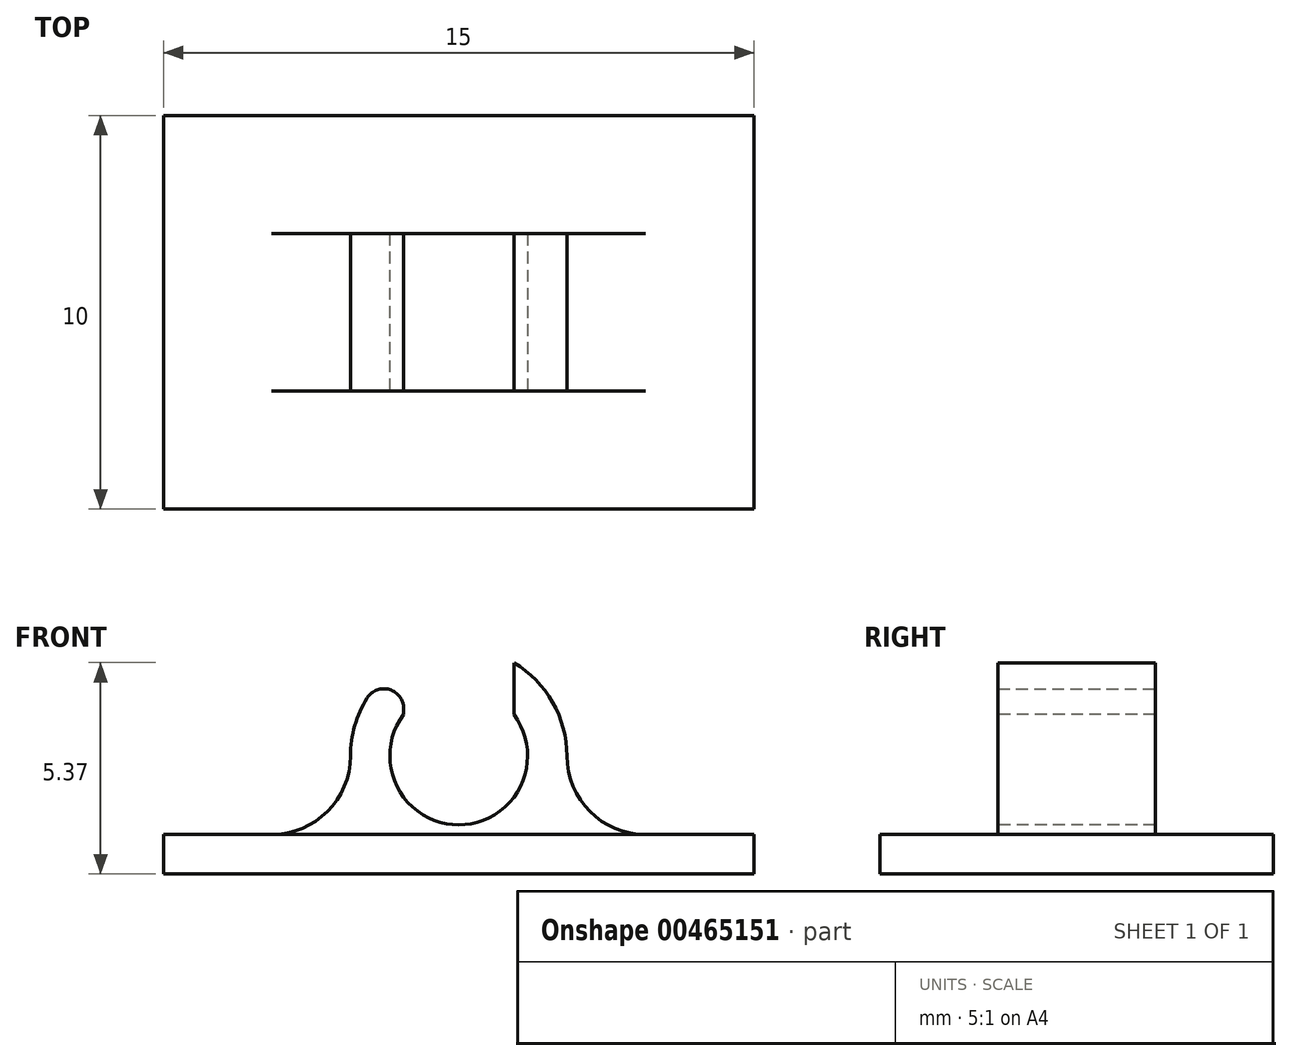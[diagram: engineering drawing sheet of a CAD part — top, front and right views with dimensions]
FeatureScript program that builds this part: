
annotation { "Feature Type Name" : "Feature", "Feature Type Description" : "" }
export const myFeature = defineFeature(function(context is Context, id is Id, definition is map)
    precondition{}
    {
        {
            assignVariable(context, id + "F0", {"name" : "base_height", "anyValue" : 1 * mm});
        }
        {
            var Q0;
            Q0=qCreatedBy(makeId("Top.planeOp"),FACE);
            var sketch = newSketch(context, id + "F1", { "sketchPlane" : qUnion([Q0])});
            skLineSegment(sketch, "E0.bottom", {"start": v(7.5, 5) * mm, "end": v(-7.5, 5) * mm});
            skLineSegment(sketch, "E0.top", {"start": v(7.5, -5) * mm, "end": v(-7.5, -5) * mm});
            skLineSegment(sketch, "E0.left", {"start": v(7.5, 5) * mm, "end": v(7.5, -5) * mm});
            skLineSegment(sketch, "E0.right", {"start": v(-7.5, 5) * mm, "end": v(-7.5, -5) * mm});
            skPoint(sketch, "E0.middle", {"position": v(0, 0) * mm});
            skSolve(sketch);
        }
        {
            var Q0;
            Q0=makeQuery(id+"F1.imprint","IMPRINT",FACE,{"disambiguationData":[TD([[makeQuery(id+"F1.imprint","IMPRINT",EDGE,{"derivedFrom":sQuery(id+"F1.wireOp",EDGE,"E0.bottom")}),1.0]])]});
            extrude(context, id + "F2", {"entities" : qUnion([Q0]), "depth" : getVariable(context, 'base_height')});
        }
        {
            var Q0;
            Q0=qCreatedBy(makeId("Front.planeOp"),FACE);
            var sketch = newSketch(context, id + "F3", { "sketchPlane" : qUnion([Q0])});
            skCircle(sketch, "E1", {"center": v(0, 3) * mm, "radius": 2.75 * mm});
            skSolve(sketch);
        }
        {
            var Q0;
            Q0=makeQuery(id+"F3.imprint","IMPRINT",FACE,{"disambiguationData":[TD([[makeQuery(id+"F3.imprint","IMPRINT",EDGE,{"derivedFrom":sQuery(id+"F3.wireOp",EDGE,"E1")}),1.0]])]});
            extrude(context, id + "F4", {"entities" : qUnion([Q0]), "operationType" : NewBodyOperationType.ADD, "endBound" : BoundingType.SYMMETRIC, "depth" : 4 * mm});
        }
        {
            var Q0;
            Q0=makeQuery(id+"F4.opExtrude","CAP_FACE",FACE,{"disambiguationData":[OSD([sQuery(id+"F3.wireOp",EDGE,"E1")])],"isStart":false});
            var sketch = newSketch(context, id + "F5", { "sketchPlane" : qUnion([Q0])});
            skCircle(sketch, "E2", {"center": v(0, 3) * mm, "radius": 1.75 * mm});
            skLineSegment(sketch, "E3.bottom", {"start": v(1.4, 6.4) * mm, "end": v(-1.4, 6.4) * mm});
            skLineSegment(sketch, "E3.top", {"start": v(1.4, 3.1) * mm, "end": v(-1.4, 3.1) * mm});
            skLineSegment(sketch, "E3.left", {"start": v(1.4, 6.4) * mm, "end": v(1.4, 3.1) * mm});
            skLineSegment(sketch, "E3.right", {"start": v(-1.4, 6.4) * mm, "end": v(-1.4, 3.1) * mm});
            skPoint(sketch, "E3.middle", {"position": v(0, 4.75) * mm});
            skSolve(sketch);
        }
        {
            var Q0;
            {var subQ5=sQuery(id+"F5.wireOp",EDGE,"E3.top");Q0=makeQuery(id+"F5.imprint","IMPRINT",FACE,{"disambiguationData":[TD([[makeQuery(id+"F5.imprint","IMPRINT",EDGE,{"derivedFrom":subQ5}),1.0]])]});}
            var Q1;
            {var subQ5=sQuery(id+"F5.wireOp",EDGE,"E3.top");Q1=makeQuery(id+"F5.imprint","IMPRINT",FACE,{"disambiguationData":[TD([[makeQuery(id+"F5.imprint","IMPRINT",EDGE,{"derivedFrom":subQ5}),-1.0]])]});}
            var Q2;
            {var subQ0=sQuery(id+"F5.wireOp",EDGE,"E3.left");var subQ1=sQuery(id+"F5.wireOp",EDGE,"E2");var subQ2=makeQuery(id+"F5.imprint","INTERSECT",VERTEX,{"derivedFrom":[subQ1,subQ0]});Q2=makeQuery(id+"F5.imprint","IMPRINT",FACE,{"disambiguationData":[TD([[makeQuery(id+"F5.imprint","IMPRINT",EDGE,{"disambiguationData":[TD([[subQ2,-1.0]])],"derivedFrom":subQ1}),-1.0]])]});}
            extrude(context, id + "F6", {"entities" : qUnion([Q0, Q1, Q2]), "operationType" : NewBodyOperationType.REMOVE, "endBound" : BoundingType.UP_TO_NEXT, "oppositeDirection" : true, "depth" : 25 * mm});
        }
        {
            var Q0;
            Q0=makeQuery(id+"F4.boolean.opBoolean","INTERSECT",EDGE,{"disambiguationData":[OD(0.0)],"derivedFrom":[makeQuery(id+"F2.opExtrude","CAP_FACE",FACE,{"disambiguationData":[OSD([sQuery(id+"F1.wireOp",EDGE,"E0.bottom"),sQuery(id+"F1.wireOp",EDGE,"E0.top"),sQuery(id+"F1.wireOp",EDGE,"E0.left"),sQuery(id+"F1.wireOp",EDGE,"E0.right")])],"isStart":false}),makeQuery(id+"F4.opExtrude","SWEPT_FACE",FACE,{"disambiguationData":[OSD([sQuery(id+"F3.wireOp",EDGE,"E1")])]})]});
            var Q1;
            Q1=makeQuery(id+"F4.boolean.opBoolean","INTERSECT",EDGE,{"disambiguationData":[OD(1.0)],"derivedFrom":[makeQuery(id+"F2.opExtrude","CAP_FACE",FACE,{"disambiguationData":[OSD([sQuery(id+"F1.wireOp",EDGE,"E0.bottom"),sQuery(id+"F1.wireOp",EDGE,"E0.top"),sQuery(id+"F1.wireOp",EDGE,"E0.left"),sQuery(id+"F1.wireOp",EDGE,"E0.right")])],"isStart":false}),makeQuery(id+"F4.opExtrude","SWEPT_FACE",FACE,{"disambiguationData":[OSD([sQuery(id+"F3.wireOp",EDGE,"E1")])]})]});
            fillet(context, id + "F7", {"entities" : qUnion([Q0, Q1]), "radius" : 2 * mm, "tangentPropagation" : true, "allowEdgeOverflow" : false});
        }
        {
            var Q0;
            Q0=makeQuery(id+"F6.boolean.opBoolean","COPY",EDGE,{"derivedFrom":makeQuery(id+"F6.opExtrude","SWEPT_EDGE",EDGE,{"disambiguationData":[OSD([sQuery(id+"F3.wireOp",EDGE,"E1"),sQuery(id+"F5.wireOp",EDGE,"E3.right")])]})});
            var Q1;
            Q1=makeQuery(id+"F6.boolean.opBoolean","COPY",EDGE,{"derivedFrom":makeQuery(id+"F6.opExtrude","SWEPT_EDGE",EDGE,{"disambiguationData":[OSD([sQuery(id+"F3.wireOp",EDGE,"E1"),sQuery(id+"F5.wireOp",EDGE,"E3.left")])]})});
            fillet(context, id + "F8", {"entities" : qUnion([Q0, Q1]), "radius" : 0.5 * mm, "tangentPropagation" : true, "allowEdgeOverflow" : false});
        }
    });
